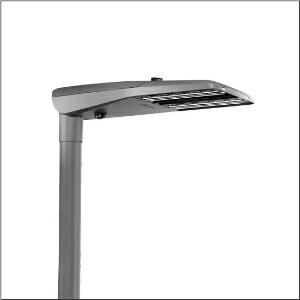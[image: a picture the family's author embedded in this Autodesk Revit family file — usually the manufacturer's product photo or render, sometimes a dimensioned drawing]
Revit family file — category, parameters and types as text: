
# Revit family: streetlight_sl_11_iq_midi___st1_0ab_5xc3n51y08le_be24
name_source: partatom
category: Lighting Fixtures
units: mm (PartAtom-declared; Revit-internal decimal feet)

## family parameters
Cut with Voids When Loaded = No
Host = Face
Light Source = No
Part Type = Normal
Room Calculation Point = No
Round Connector Dimension = Use Diameter
Shared = No

## types (1)
- --- (1 x LED, 7760 lm, 59.4 W, 3000K)
    Apparent Load = 59 VA
    CIE Flux Codes = 29 63 95 100 100
    Color Rendering = 70
    Color Temperature = 3000K
    Default Elevation = 1800 mm
    Description = Streetlight SL 11 iQ midi, mast luminaire, primary light control with 3 zone facetted reflector, of plastic, silver coated, highly specular, primary optical cover: cover, of PMMA, transparent, light distribution: ST1.0aB, light emission: direct distribution, primary light characteristic: asymmetric, installation type: post-top, side-entry, LED, High Power LED, rated luminous flux: 7.760lm, luminous efficacy: 131lm/W, light colour: 730, colour temperature: 3000K, control: presetting dimming logarithmic, Street-Remote, Auto-Match, Temp-Guard, Lumen-Switch, Night-Set, Smart-Wire, Light-Fading, Desk-Remote (wireless, voltage-free reading and setting of iQ features in the workshop via application-optimized NFC function/RFID function), optimised constant luminous flux control (CLO 2.0), with cable H07RN-F 5x 1.5mm², mains connection: 230..240V, AC, 50/60Hz, connection cable pre-assembled, cable length: 8,5m, start of lifetime: 59W, end of service life: 62W, reduction: 29W, luminaire housing, of diecast aluminium, powder-coated, Siteco® metallic grey (DB 702S), please order mast flange separately, inclination adjustable without tools: 0°, 5°, 10°, 15° (post-top) | 0°, -5°, -10°, -15° (side-entry), sealing non-destructively replaceable, multi-level sealing system, length: 780mm, width: 376mm, height: 118mm, mast flange for spigot size: 42mm (side-entry): 5XC10008XM4, 60/48mm (side-entry/post-top): 5XC10108XM2, 76/60mm (side-entry/post-top): 5XC10108XM1, equipment: standard, Smart Interface below and above, protection rating (complete): IP66, insulation class (complete): insulation class II (safety insulation), certification: CE, ENEC, VDE, UKCA, impact resistance: IK09, permissible operating ambient temperature for outdoor applications: -25..+50°C, standard-compliant lighting for roads and squares, Environmental Product Declaration (EPD) tested and certified by an independent institute, packaging unit: 1 piece

Light Distribution: ST1.0aB
    Height = 118 mm
    Lamp = 1 x LED
    Lamp Light Flux = 7760 lm
    Lamp Power = 59.4 W
    Lamp count = 1
    Length = 780 mm
    Luminous efficacy = 131 lm/W
    Manufacturer = Siteco
    ModVariant = No
    Model = 5XC3N51Y08LE
    Number of Poles = 1
    OnlyDefault = Yes
    Power Factor = 1
    Product Name = Streetlight SL 11 iQ midi | ST1.0aB
    Product group = mast luminaire | pylon top
    ProductGroupID = 6100
    Protection Class = Protection class II
    Protection Degree = IP 66
    RLX_Detail_Level = 1
    RLX_Emergency_Light_Flux = 0 lm
    RLX_Emergency_Type = 0
    RLX_Emergency_Type_DB = No
    RlxData = <blob elided: 69097 chars, md5=c6105e5d>
    Socket = socket
    Standby Power = 0 W
    System Light Flux = 7760 lm
    System Power = 59 W
    Type Comments = factory setting: luminous flux: 100 % | dim-lin: 254 | 521 mA
    Type Image = l_1004429.jpg
    URL = http://relux.com
    VarID = @adj_038785
    Voltage = 0 V
    Weight = 0.00 kg
    Width = 376 mm

## geometry (parser evidence)
native form markers: Blend x4, Sweep x11
no freeform markers — native parametric forms only
